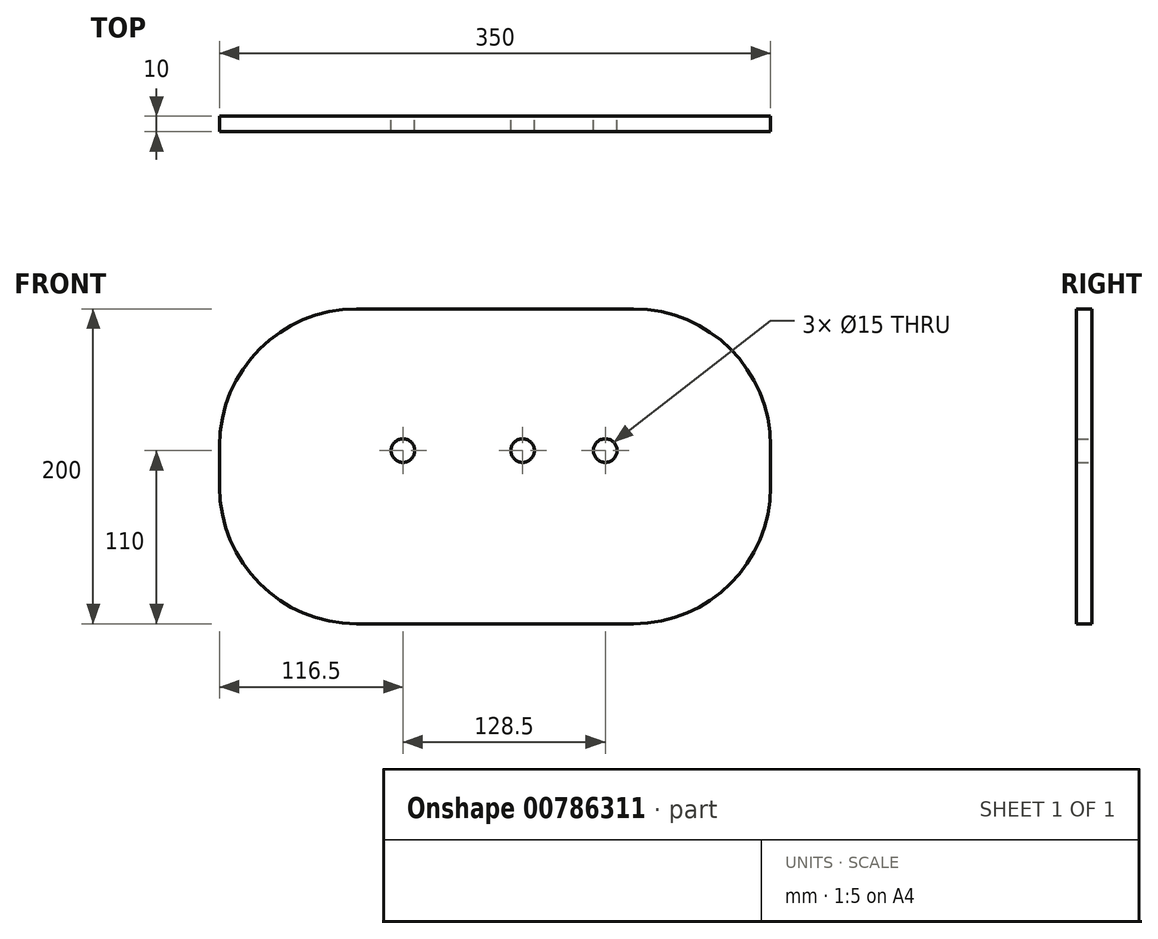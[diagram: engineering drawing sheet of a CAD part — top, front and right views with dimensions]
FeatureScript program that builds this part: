
annotation { "Feature Type Name" : "Feature", "Feature Type Description" : "" }
export const myFeature = defineFeature(function(context is Context, id is Id, definition is map)
    precondition{}
    {
        {
            var Q0;
            Q0=qCreatedBy(makeId("Front.planeOp"),FACE);
            var sketch = newSketch(context, id + "F0", { "sketchPlane" : qUnion([Q0])});
            skLineSegment(sketch, "E0.bottom", {"start": v(-175, 100) * mm, "end": v(175, 100) * mm});
            skLineSegment(sketch, "E0.top", {"start": v(-175, -100) * mm, "end": v(175, -100) * mm});
            skLineSegment(sketch, "E0.left", {"start": v(-175, 100) * mm, "end": v(-175, -100) * mm});
            skLineSegment(sketch, "E0.right", {"start": v(175, 100) * mm, "end": v(175, -100) * mm});
            skPoint(sketch, "E0.middle", {"position": v(0, 0) * mm});
            skCircle(sketch, "E1", {"center": v(70, 10) * mm, "radius": 7.5 * mm});
            skCircle(sketch, "E2", {"center": v(17.5, 10) * mm, "radius": 7.5 * mm});
            skCircle(sketch, "E3", {"center": v(-58.5, 10) * mm, "radius": 7.5 * mm});
            skSolve(sketch);
        }
        {
            var Q0;
            Q0=makeQuery(id+"F0.imprint","IMPRINT",FACE,{"disambiguationData":[TD([[makeQuery(id+"F0.imprint","IMPRINT",EDGE,{"derivedFrom":sQuery(id+"F0.wireOp",EDGE,"E0.bottom")}),-1.0]])]});
            extrude(context, id + "F1", {"entities" : qUnion([Q0]), "depth" : 10 * mm, "offsetDistance" : 25.4 * mm});
        }
        {
            var Q0;
            Q0=makeQuery(id+"F1.opExtrude","SWEPT_EDGE",EDGE,{"disambiguationData":[OSD([sQuery(id+"F0.wireOp",EDGE,"E0.bottom"),sQuery(id+"F0.wireOp",EDGE,"E0.right")])]});
            var Q1;
            Q1=makeQuery(id+"F1.opExtrude","SWEPT_EDGE",EDGE,{"disambiguationData":[OSD([sQuery(id+"F0.wireOp",EDGE,"E0.bottom"),sQuery(id+"F0.wireOp",EDGE,"E0.left")])]});
            var Q2;
            Q2=makeQuery(id+"F1.opExtrude","SWEPT_EDGE",EDGE,{"disambiguationData":[OSD([sQuery(id+"F0.wireOp",EDGE,"E0.top"),sQuery(id+"F0.wireOp",EDGE,"E0.left")])]});
            var Q3;
            Q3=makeQuery(id+"F1.opExtrude","SWEPT_EDGE",EDGE,{"disambiguationData":[OSD([sQuery(id+"F0.wireOp",EDGE,"E0.top"),sQuery(id+"F0.wireOp",EDGE,"E0.right")])]});
            fillet(context, id + "F2", {"entities" : qUnion([Q0, Q1, Q2, Q3]), "radius" : 87 * mm, "tangentPropagation" : true, "allowEdgeOverflow" : false});
        }
    });
